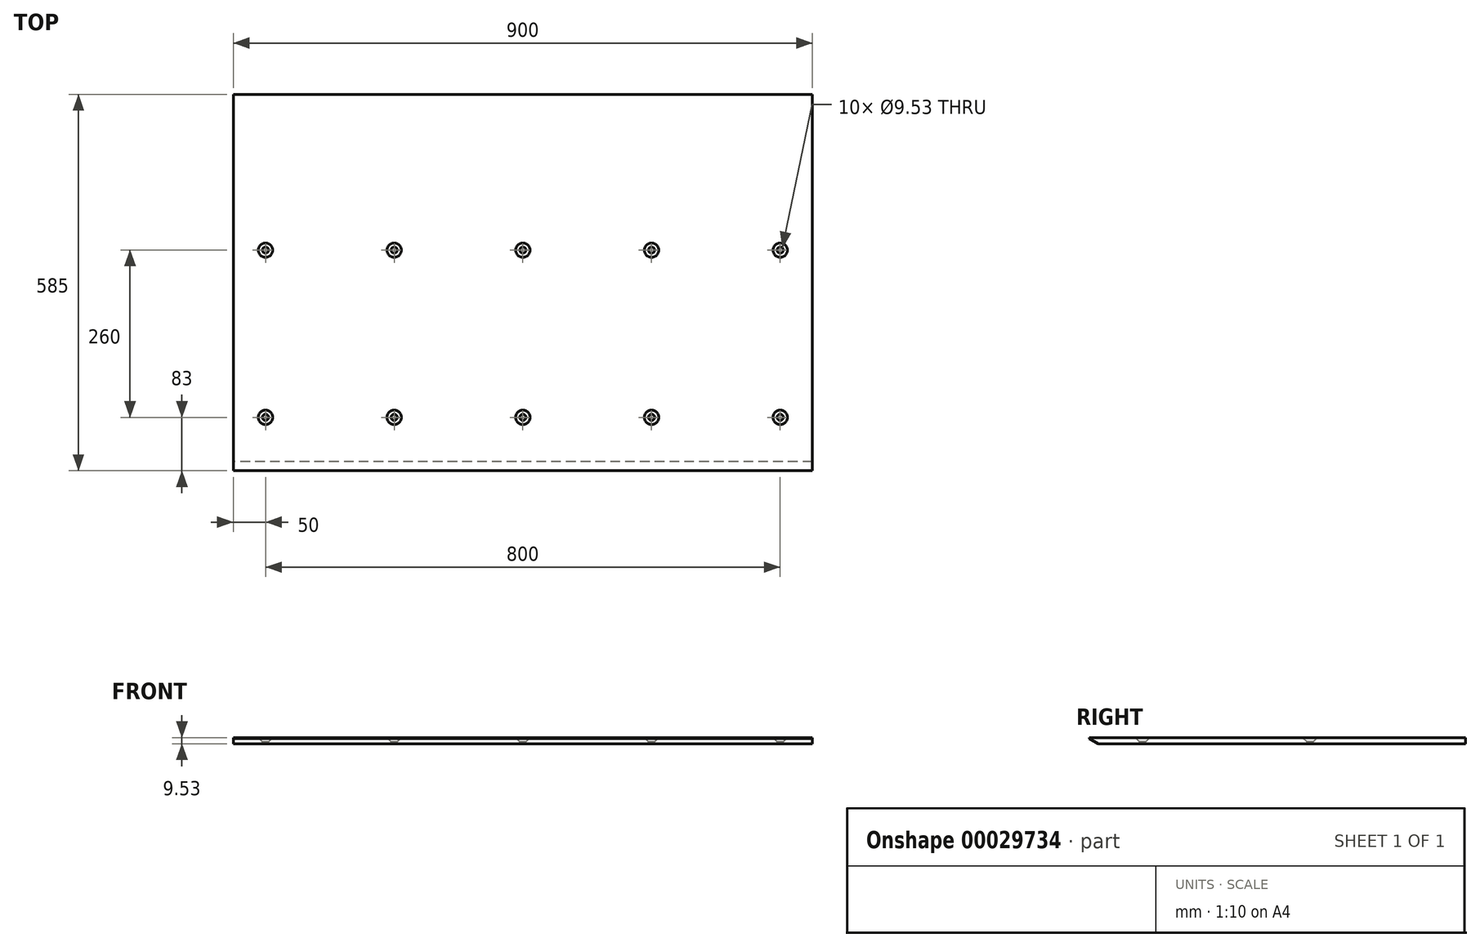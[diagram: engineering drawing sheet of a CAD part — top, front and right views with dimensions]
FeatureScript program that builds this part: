
annotation { "Feature Type Name" : "Feature", "Feature Type Description" : "" }
export const myFeature = defineFeature(function(context is Context, id is Id, definition is map)
    precondition{}
    {
        {
            var Q0;
            Q0=qCreatedBy(makeId("Top.planeOp"),FACE);
            var sketch = newSketch(context, id + "F0", { "sketchPlane" : qUnion([Q0])});
            skLineSegment(sketch, "E0.rect.bottom", {"start": v(-450, 292.5) * mm, "end": v(450, 292.5) * mm});
            skLineSegment(sketch, "E0.rect.top", {"start": v(-450, -292.5) * mm, "end": v(450, -292.5) * mm});
            skLineSegment(sketch, "E0.rect.left", {"start": v(-450, 292.5) * mm, "end": v(-450, -292.5) * mm});
            skLineSegment(sketch, "E0.rect.right", {"start": v(450, 292.5) * mm, "end": v(450, -292.5) * mm});
            skPoint(sketch, "E0.rect.middle", {"position": v(0, 0) * mm});
            skLineSegment(sketch, "E1.0", {"start": v(-450, 50.5) * mm, "end": v(1350, 50.5) * mm, "construction": true});
            skLineSegment(sketch, "E2.0", {"start": v(-450, -209.5) * mm, "end": v(1350, -209.5) * mm, "construction": true});
            skLineSegment(sketch, "E3", {"start": v(0, 428.62) * mm, "end": v(0, -394.87) * mm, "construction": true});
            skLineSegment(sketch, "E4.0", {"start": v(-200, 428.62) * mm, "end": v(-200, -394.87) * mm, "construction": true});
            skLineSegment(sketch, "E5.0", {"start": v(-400, 428.62) * mm, "end": v(-400, -394.87) * mm, "construction": true});
            skPoint(sketch, "E6", {"position": v(-400, 50.5) * mm});
            skPoint(sketch, "E7", {"position": v(-400, -209.5) * mm});
            skPoint(sketch, "E8", {"position": v(-200, -209.5) * mm});
            skPoint(sketch, "E9", {"position": v(-200, 50.5) * mm});
            skPoint(sketch, "E10", {"position": v(0, 50.5) * mm});
            skPoint(sketch, "E11", {"position": v(0, -209.5) * mm});
            skPoint(sketch, "E12.MirrorP", {"position": v(200, 50.5) * mm});
            skPoint(sketch, "E13.MirrorP", {"position": v(200, -209.5) * mm});
            skPoint(sketch, "E14.MirrorP", {"position": v(400, -209.5) * mm});
            skPoint(sketch, "E15.MirrorP", {"position": v(400, 50.5) * mm});
            skSolve(sketch);
        }
        {
            var Q0;
            Q0 = qSketchRegion(id + "F0", true);
            extrude(context, id + "F1", {"entities" : qUnion([Q0]), "oppositeDirection" : true, "depth" : 9.52 * mm});
        }
        {
            var Q0;
            Q0=sQuery(id+"F0.wireOp",VERTEX,"E6");
            var Q1;
            Q1=sQuery(id+"F0.wireOp",VERTEX,"E7");
            var Q2;
            Q2=sQuery(id+"F0.wireOp",VERTEX,"E9");
            var Q3;
            Q3=sQuery(id+"F0.wireOp",VERTEX,"E8");
            var Q4;
            Q4=sQuery(id+"F0.wireOp",VERTEX,"E10");
            var Q5;
            Q5=sQuery(id+"F0.wireOp",VERTEX,"E11");
            var Q6;
            Q6=sQuery(id+"F0.wireOp",VERTEX,"E12.MirrorP");
            var Q7;
            Q7=sQuery(id+"F0.wireOp",VERTEX,"E13.MirrorP");
            var Q8;
            Q8=sQuery(id+"F0.wireOp",VERTEX,"E14.MirrorP");
            var Q9;
            Q9=sQuery(id+"F0.wireOp",VERTEX,"E15.MirrorP");
            var Q10;
            Q10=makeQuery(id+"F1.opExtrude","SWEPT_BODY",BODY,{"disambiguationData":[OSD([sQuery(id+"F0.wireOp",EDGE,"E0.rect.bottom"),sQuery(id+"F0.wireOp",EDGE,"E0.rect.top"),sQuery(id+"F0.wireOp",EDGE,"E0.rect.left"),sQuery(id+"F0.wireOp",EDGE,"E0.rect.right")])]});
            hole(context, id + "F2", {"style" : HoleStyle.C_SINK, "holeDiameter" : 9.52 * mm, "cSinkDiameter" : 22.35 * mm, "endStyle" : HoleEndStyle.THROUGH, "locations" : qUnion([Q0, Q1, Q2, Q3, Q4, Q5, Q6, Q7, Q8, Q9]), "scope" : qUnion([Q10]), "cSinkAngle" : 90 * degree});
        }
        {
            var Q0;
            Q0=makeQuery(id+"F1.opExtrude","CAP_EDGE",EDGE,{"disambiguationData":[OSD([sQuery(id+"F0.wireOp",EDGE,"E0.rect.top")])],"isStart":false});
            chamfer(context, id + "F3", {"entities" : qUnion([Q0]), "chamferType" : ChamferType.OFFSET_ANGLE, "width" : 13.97 * mm, "oppositeDirection" : true, "angle" : 30 * degree, "tangentPropagation" : true});
        }
    });
